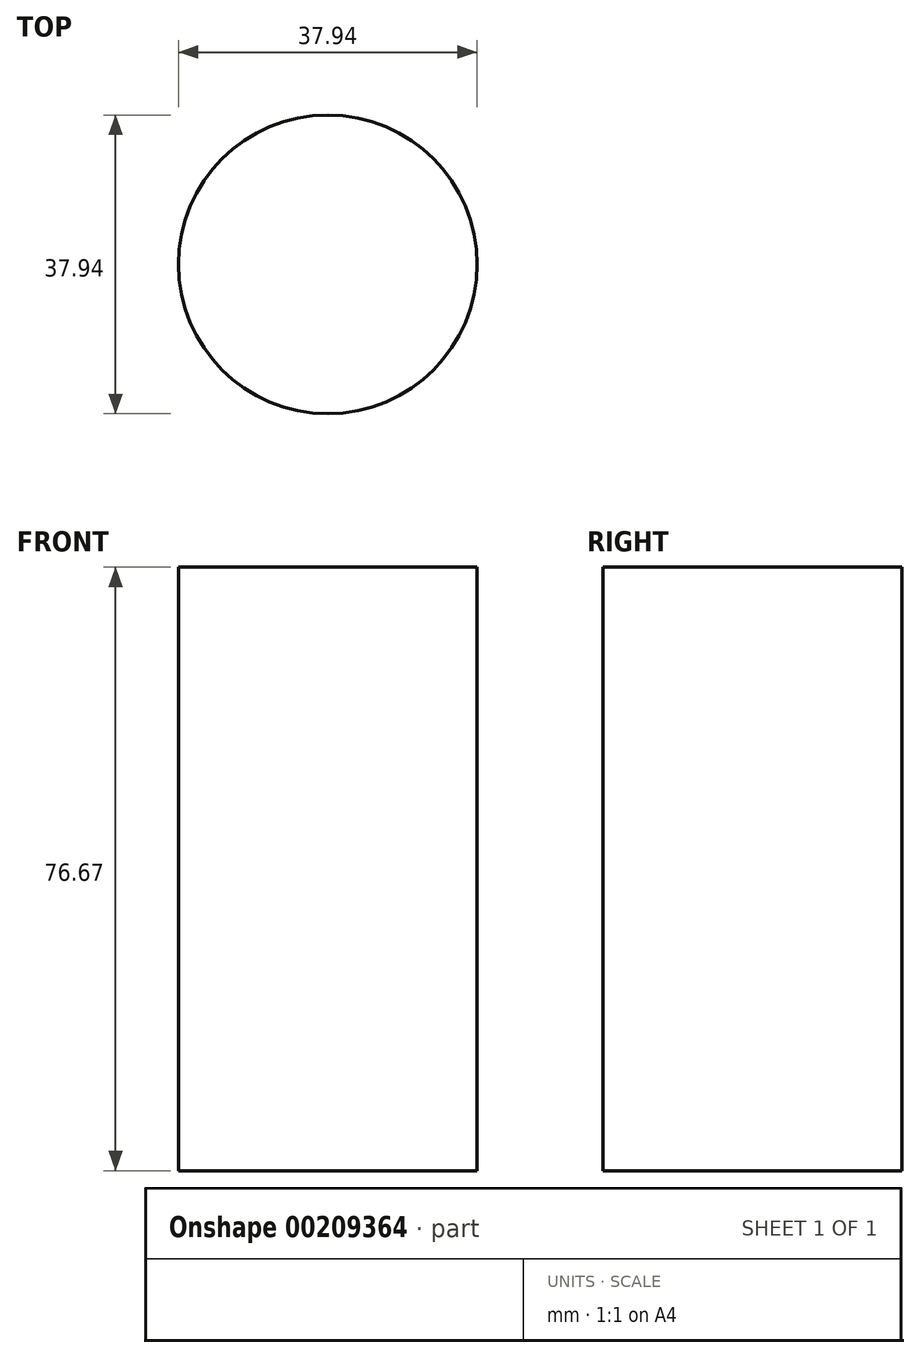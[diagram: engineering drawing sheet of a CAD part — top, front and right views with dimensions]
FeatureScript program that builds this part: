
annotation { "Feature Type Name" : "Feature", "Feature Type Description" : "" }
export const myFeature = defineFeature(function(context is Context, id is Id, definition is map)
    precondition{}
    {
        {
            var Q0;
            Q0=qCreatedBy(makeId("Top.planeOp"),FACE);
            var sketch = newSketch(context, id + "F0", { "sketchPlane" : qUnion([Q0])});
            skCircle(sketch, "E0", {"center": v(-26.9, 39.12) * mm, "radius": 18.97 * mm});
            skCircle(sketch, "E1.1.0", {"center": v(11.7, 5.08) * mm, "radius": 18.97 * mm});
            skCircle(sketch, "E1.2.0", {"center": v(-16.84, -37.75) * mm, "radius": 18.97 * mm});
            skPoint(sketch, "E1.center", {"position": v(-27.1, 0) * mm});
            skLineSegment(sketch, "E1.anchor1", {"start": v(-27.1, 0) * mm, "end": v(-26.9, 39.12) * mm, "construction": true});
            skLineSegment(sketch, "E1.anchor2", {"start": v(-27.1, 0) * mm, "end": v(-16.84, -37.75) * mm, "construction": true});
            skSolve(sketch);
        }
        {
            var Q0;
            Q0=sQuery(id+"F0.wireOp",EDGE,"E1.1.0");
            extrude(context, id + "F1", {"bodyType" : ToolBodyType.SURFACE, "surfaceEntities" : qUnion([Q0]), "depth" : 76.67 * mm});
        }
    });
